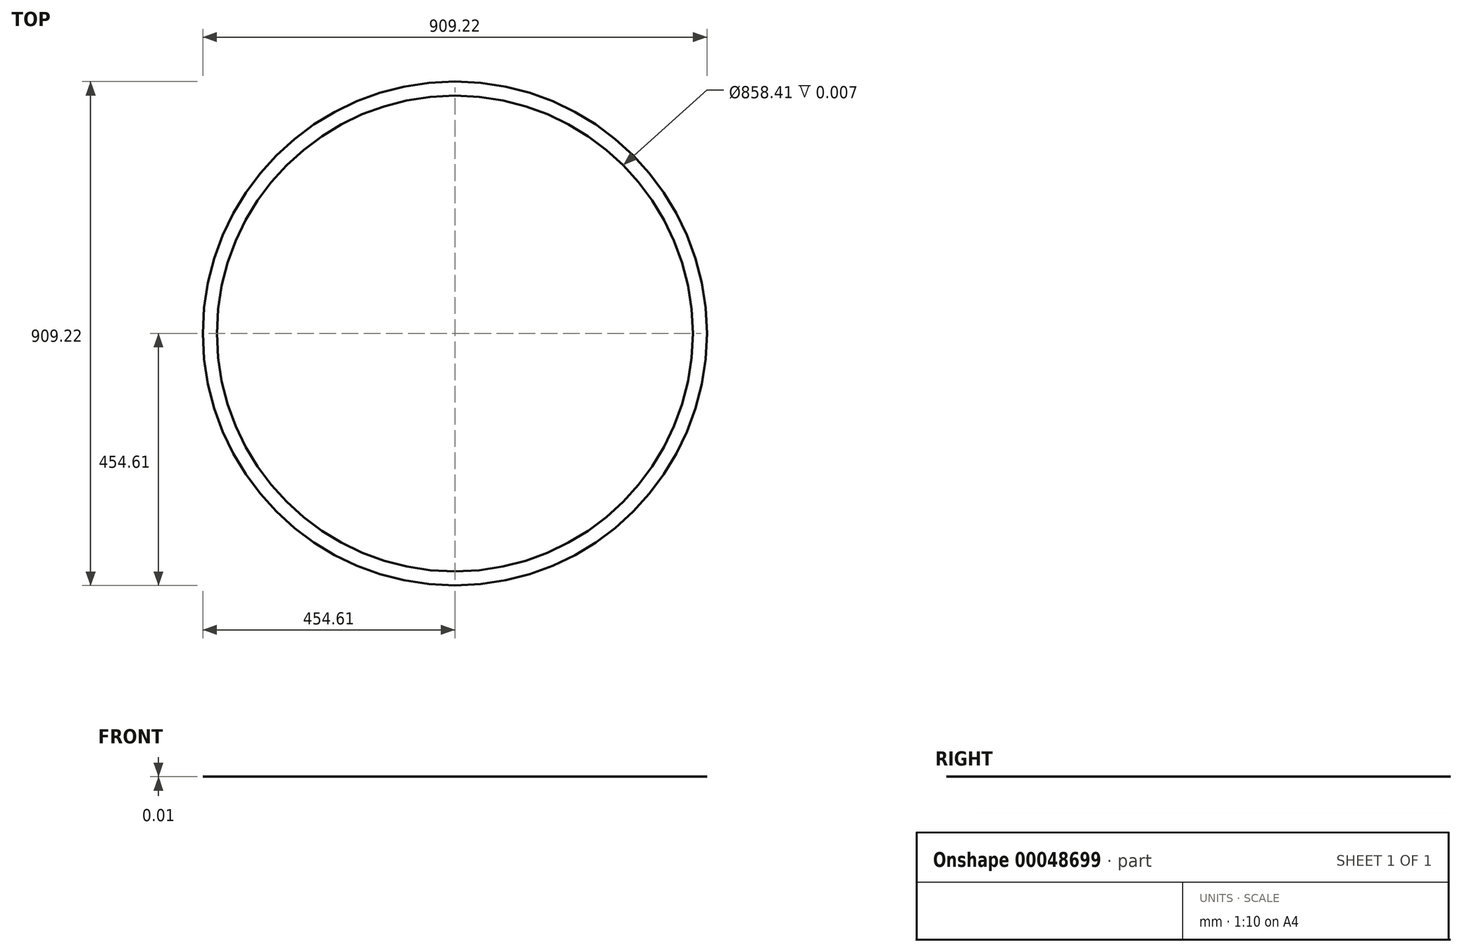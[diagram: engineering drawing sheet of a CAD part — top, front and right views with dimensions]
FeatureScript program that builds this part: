
annotation { "Feature Type Name" : "Feature", "Feature Type Description" : "" }
export const myFeature = defineFeature(function(context is Context, id is Id, definition is map)
    precondition{}
    {
        {
            var Q0;
            Q0=qCreatedBy(makeId("Top.planeOp"),FACE);
            var sketch = newSketch(context, id + "F0", { "sketchPlane" : qUnion([Q0])});
            skCircle(sketch, "E0", {"center": v(0, 0) * mm, "radius": 454.6 * mm});
            skCircle(sketch, "E1", {"center": v(0, 0) * mm, "radius": 429.2 * mm});
            skSolve(sketch);
        }
        {
            var Q0;
            Q0 = qSketchRegion(id + "F0", true);
            extrude(context, id + "F1", {"entities" : qUnion([Q0]), "depth" : 3 / 457.2 * mm});
        }
    });
